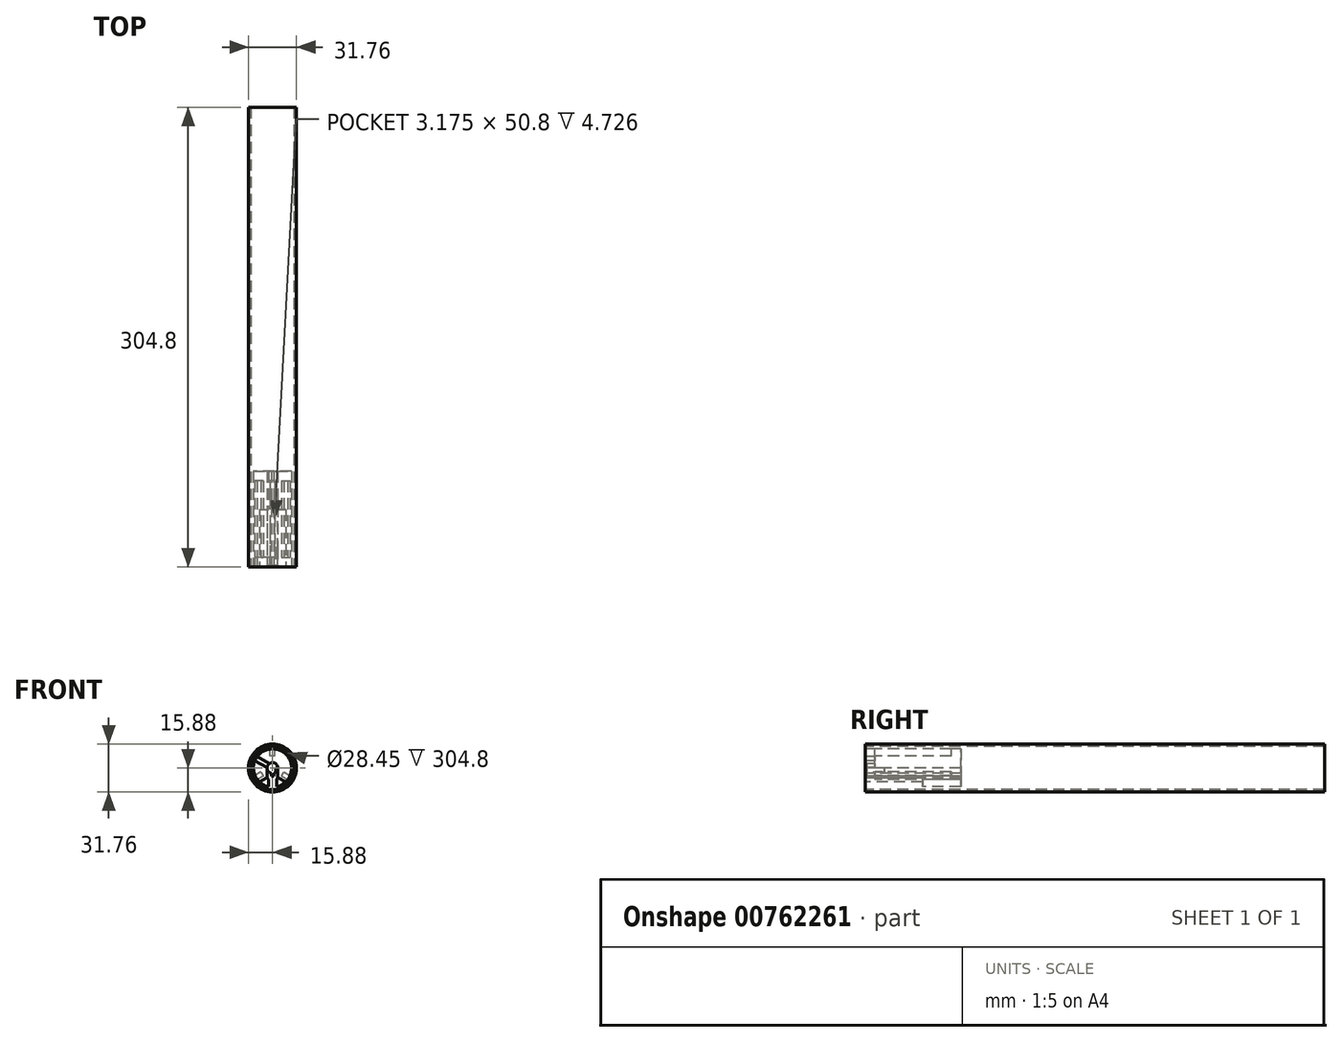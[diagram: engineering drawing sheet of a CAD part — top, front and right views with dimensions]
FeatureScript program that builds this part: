
annotation { "Feature Type Name" : "Feature", "Feature Type Description" : "" }
export const myFeature = defineFeature(function(context is Context, id is Id, definition is map)
    precondition{}
    {
        {
            var Q0;
            Q0=qCreatedBy(makeId("Front.planeOp"),FACE);
            var sketch = newSketch(context, id + "F0", { "sketchPlane" : qUnion([Q0])});
            skCircle(sketch, "E0", {"center": v(0, 0) * mm, "radius": 15.88 * mm});
            skCircle(sketch, "E1", {"center": v(0, 0) * mm, "radius": 14.22 * mm});
            skSolve(sketch);
        }
        {
            var Q0;
            Q0=makeQuery(id+"F0.imprint","IMPRINT",FACE,{"disambiguationData":[TD([[makeQuery(id+"F0.imprint","IMPRINT",EDGE,{"derivedFrom":sQuery(id+"F0.wireOp",EDGE,"E0")}),1.0]])]});
            extrude(context, id + "F1", {"entities" : qUnion([Q0]), "oppositeDirection" : true, "depth" : 304.8 * mm, "offsetDistance" : 25.4 * mm});
        }
        {
            var Q0;
            Q0=qCreatedBy(makeId("Front.planeOp"),FACE);
            var sketch = newSketch(context, id + "F2", { "sketchPlane" : qUnion([Q0])});
            skCircle(sketch, "E2", {"center": v(0, 0) * mm, "radius": 12.7 * mm});
            skCircle(sketch, "E3.0.0", {"center": v(0, 0) * mm, "radius": 15.88 * mm});
            skCircle(sketch, "E4.0", {"center": v(0, 0) * mm, "radius": 14.22 * mm});
            skLineSegment(sketch, "E5", {"start": v(0, 14.22) * mm, "end": v(0, 7.87) * mm});
            skLineSegment(sketch, "E6", {"start": v(0, 7.87) * mm, "end": v(-1.59, 7.87) * mm});
            skLineSegment(sketch, "E7", {"start": v(0, 7.87) * mm, "end": v(1.59, 7.87) * mm});
            skLineSegment(sketch, "E8", {"start": v(-1.59, 7.87) * mm, "end": v(-1.59, 14.14) * mm});
            skLineSegment(sketch, "E9", {"start": v(1.59, 7.87) * mm, "end": v(1.59, 14.14) * mm});
            skLineSegment(sketch, "E10", {"start": v(-1.59, 14.14) * mm, "end": v(1.59, 14.14) * mm});
            skLineSegment(sketch, "E11.1.0", {"start": v(-6.03, -5.31) * mm, "end": v(-11.45, -8.44) * mm});
            skLineSegment(sketch, "E11.1.1", {"start": v(-6.82, -3.94) * mm, "end": v(-6.03, -5.31) * mm});
            skLineSegment(sketch, "E11.1.2", {"start": v(-6.82, -3.94) * mm, "end": v(-7.61, -2.56) * mm});
            skLineSegment(sketch, "E11.1.3", {"start": v(-7.61, -2.56) * mm, "end": v(-13.04, -5.7) * mm});
            skLineSegment(sketch, "E11.1.4", {"start": v(-11.45, -8.44) * mm, "end": v(-13.04, -5.7) * mm});
            skLineSegment(sketch, "E11.2.0", {"start": v(7.61, -2.56) * mm, "end": v(13.04, -5.7) * mm});
            skLineSegment(sketch, "E11.2.1", {"start": v(6.82, -3.94) * mm, "end": v(7.61, -2.56) * mm});
            skLineSegment(sketch, "E11.2.2", {"start": v(6.82, -3.94) * mm, "end": v(6.03, -5.31) * mm});
            skLineSegment(sketch, "E11.2.3", {"start": v(6.03, -5.31) * mm, "end": v(11.45, -8.44) * mm});
            skLineSegment(sketch, "E11.2.4", {"start": v(13.04, -5.7) * mm, "end": v(11.45, -8.44) * mm});
            skCircle(sketch, "E12", {"center": v(0, 0) * mm, "radius": 3.56 * mm});
            skLineSegment(sketch, "E13", {"start": v(3.56, 0) * mm, "end": v(3.56, -12.2) * mm});
            skLineSegment(sketch, "E14", {"start": v(-3.56, 0) * mm, "end": v(-3.56, -12.2) * mm});
            skLineSegment(sketch, "E15", {"start": v(0, -2.16) * mm, "end": v(0.77, -2.16) * mm});
            skLineSegment(sketch, "E16", {"start": v(0.77, -2.16) * mm, "end": v(0.77, -5.34) * mm});
            skLineSegment(sketch, "E17", {"start": v(0.77, -5.34) * mm, "end": v(0, -5.34) * mm});
            skLineSegment(sketch, "E18", {"start": v(0, -2.16) * mm, "end": v(-0.75, -2.16) * mm});
            skLineSegment(sketch, "E19", {"start": v(-0.75, -2.16) * mm, "end": v(-0.75, -5.34) * mm});
            skLineSegment(sketch, "E20", {"start": v(-0.75, -5.34) * mm, "end": v(0, -5.34) * mm});
            skLineSegment(sketch, "E21", {"start": v(-3.08, 1.78) * mm, "end": v(-2.57, 1.49) * mm});
            skCircle(sketch, "E22", {"center": v(0, 0) * mm, "radius": 2.97 * mm});
            skLineSegment(sketch, "E23", {"start": v(-1.78, 2.86) * mm, "end": v(-1.38, 2.63) * mm});
            skLineSegment(sketch, "E24", {"start": v(-3.37, 0.11) * mm, "end": v(-2.97, -0.12) * mm});
            skLineSegment(sketch, "E25", {"start": v(-1.78, 2.86) * mm, "end": v(-10.12, 7.68) * mm});
            skLineSegment(sketch, "E26", {"start": v(-3.37, 0.11) * mm, "end": v(-11.7, 4.93) * mm});
            skLineSegment(sketch, "E27.trimOffspring", {"start": v(-2.57, 1.49) * mm, "end": v(-3.08, 1.78) * mm});
            skLineSegment(sketch, "E28", {"start": v(3.56, 0) * mm, "end": v(2.29, 0) * mm});
            skLineSegment(sketch, "E29", {"start": v(2.29, 0) * mm, "end": v(2.29, -12.5) * mm});
            skLineSegment(sketch, "E30", {"start": v(8.74, -9.22) * mm, "end": v(3.56, -6.2) * mm});
            skPoint(sketch, "E30.startSnap0", {"position": v(8.74, -6.88) * mm});
            skLineSegment(sketch, "E31", {"start": v(3.56, -6.2) * mm, "end": v(3.56, -12.2) * mm});
            skLineSegment(sketch, "E32", {"start": v(-8.74, -9.22) * mm, "end": v(-3.56, -6.23) * mm});
            skPoint(sketch, "E32.startSnap0", {"position": v(-8.74, -6.88) * mm});
            skLineSegment(sketch, "E33", {"start": v(-3.56, -6.23) * mm, "end": v(-3.56, -12.2) * mm});
            skLineSegment(sketch, "E34", {"start": v(3.56, -6.2) * mm, "end": v(2.75, -7.58) * mm});
            skLineSegment(sketch, "E35", {"start": v(2.75, -7.58) * mm, "end": v(3.56, -8.05) * mm});
            skLineSegment(sketch, "E36", {"start": v(-3.56, -6.23) * mm, "end": v(-2.75, -7.62) * mm});
            skLineSegment(sketch, "E37", {"start": v(-2.75, -7.62) * mm, "end": v(-3.56, -8.09) * mm});
            skLineSegment(sketch, "E38", {"start": v(-2.75, -7.62) * mm, "end": v(-2.75, -12.4) * mm});
            skLineSegment(sketch, "E39", {"start": v(2.75, -7.58) * mm, "end": v(2.75, -12.4) * mm});
            skSolve(sketch);
        }
        {
            var Q0;
            {var subQ1=sQuery(id+"F2.wireOp",EDGE,"E6");Q0=makeQuery(id+"F2.imprint","IMPRINT",FACE,{"disambiguationData":[TD([[makeQuery(id+"F2.imprint","IMPRINT",EDGE,{"derivedFrom":subQ1}),1.0]])]});}
            var Q1;
            {var subQ4=sQuery(id+"F2.wireOp",EDGE,"E15");Q1=makeQuery(id+"F2.imprint","IMPRINT",FACE,{"disambiguationData":[TD([[makeQuery(id+"F2.imprint","IMPRINT",EDGE,{"derivedFrom":subQ4}),1.0]])]});}
            var Q2;
            {var subQ0=sQuery(id+"F2.wireOp",EDGE,"E17");Q2=makeQuery(id+"F2.imprint","IMPRINT",FACE,{"disambiguationData":[TD([[makeQuery(id+"F2.imprint","IMPRINT",EDGE,{"derivedFrom":subQ0}),-1.0]])]});}
            var Q3;
            {var subQ1=sQuery(id+"F2.wireOp",EDGE,"E15");Q3=makeQuery(id+"F2.imprint","IMPRINT",FACE,{"disambiguationData":[TD([[makeQuery(id+"F2.imprint","IMPRINT",EDGE,{"derivedFrom":subQ1}),-1.0]])]});}
            var Q4;
            {var subQ0=sQuery(id+"F2.wireOp",EDGE,"E13");Q4=makeQuery(id+"F2.imprint","IMPRINT",FACE,{"disambiguationData":[TD([[makeQuery(id+"F2.imprint","IMPRINT",EDGE,{"derivedFrom":subQ0}),-1.0]])]});}
            var Q5;
            {var subQ1=sQuery(id+"F2.wireOp",EDGE,"E11.1.1");Q5=makeQuery(id+"F2.imprint","IMPRINT",FACE,{"disambiguationData":[TD([[makeQuery(id+"F2.imprint","IMPRINT",EDGE,{"derivedFrom":subQ1}),-1.0]])]});}
            var Q6;
            {var subQ5=sQuery(id+"F2.wireOp",EDGE,"E7");Q6=makeQuery(id+"F2.imprint","IMPRINT",FACE,{"disambiguationData":[TD([[makeQuery(id+"F2.imprint","IMPRINT",EDGE,{"derivedFrom":subQ5}),1.0]])]});}
            var Q7;
            {var subQ5=sQuery(id+"F2.wireOp",EDGE,"E6");Q7=makeQuery(id+"F2.imprint","IMPRINT",FACE,{"disambiguationData":[TD([[makeQuery(id+"F2.imprint","IMPRINT",EDGE,{"derivedFrom":subQ5}),-1.0]])]});}
            var Q8;
            {var subQ1=sQuery(id+"F2.wireOp",EDGE,"E11.2.1");Q8=makeQuery(id+"F2.imprint","IMPRINT",FACE,{"disambiguationData":[TD([[makeQuery(id+"F2.imprint","IMPRINT",EDGE,{"derivedFrom":subQ1}),-1.0]])]});}
            var Q9;
            {var subQ0=sQuery(id+"F2.wireOp",EDGE,"E25");var subQ1=sQuery(id+"F2.wireOp",EDGE,"E2");var subQ2=makeQuery(id+"F2.imprint","INTERSECT",VERTEX,{"derivedFrom":[subQ1,subQ0]});Q9=makeQuery(id+"F2.imprint","IMPRINT",FACE,{"disambiguationData":[TD([[makeQuery(id+"F2.imprint","IMPRINT",EDGE,{"disambiguationData":[TD([[subQ2,-1.0]])],"derivedFrom":subQ1}),1.0]])]});}
            var Q10;
            {var subQ0=sQuery(id+"F2.wireOp",EDGE,"E23");Q10=makeQuery(id+"F2.imprint","IMPRINT",FACE,{"disambiguationData":[TD([[makeQuery(id+"F2.imprint","IMPRINT",EDGE,{"derivedFrom":subQ0}),1.0]])]});}
            var Q11;
            {var subQ0=sQuery(id+"F2.wireOp",EDGE,"E23");Q11=makeQuery(id+"F2.imprint","IMPRINT",FACE,{"disambiguationData":[TD([[makeQuery(id+"F2.imprint","IMPRINT",EDGE,{"derivedFrom":subQ0}),-1.0]])]});}
            var Q12;
            {var subQ1=sQuery(id+"F2.wireOp",EDGE,"E24");Q12=makeQuery(id+"F2.imprint","IMPRINT",FACE,{"disambiguationData":[TD([[makeQuery(id+"F2.imprint","IMPRINT",EDGE,{"derivedFrom":subQ1}),1.0]])]});}
            var Q13;
            {var subQ0=sQuery(id+"F2.wireOp",EDGE,"E24");Q13=makeQuery(id+"F2.imprint","IMPRINT",FACE,{"disambiguationData":[TD([[makeQuery(id+"F2.imprint","IMPRINT",EDGE,{"derivedFrom":subQ0}),-1.0]])]});}
            var Q14;
            {var subQ0=sQuery(id+"F2.wireOp",EDGE,"E19");var subQ1=sQuery(id+"F2.wireOp",EDGE,"E12");var subQ2=makeQuery(id+"F2.imprint","INTERSECT",VERTEX,{"derivedFrom":[subQ1,subQ0]});Q14=makeQuery(id+"F2.imprint","IMPRINT",FACE,{"disambiguationData":[TD([[makeQuery(id+"F2.imprint","IMPRINT",EDGE,{"disambiguationData":[TD([[subQ2,-1.0]])],"derivedFrom":subQ1}),1.0]])]});}
            var Q15;
            {var subQ0=sQuery(id+"F2.wireOp",EDGE,"E11.1.1");Q15=makeQuery(id+"F2.imprint","IMPRINT",FACE,{"disambiguationData":[TD([[makeQuery(id+"F2.imprint","IMPRINT",EDGE,{"derivedFrom":subQ0}),1.0]])]});}
            var Q16;
            {var subQ0=sQuery(id+"F2.wireOp",EDGE,"E28");var subQ1=sQuery(id+"F2.wireOp",EDGE,"E22");var subQ2=makeQuery(id+"F2.imprint","INTERSECT",VERTEX,{"derivedFrom":[subQ1,subQ0]});Q16=makeQuery(id+"F2.imprint","IMPRINT",FACE,{"disambiguationData":[TD([[makeQuery(id+"F2.imprint","IMPRINT",EDGE,{"disambiguationData":[TD([[subQ2,1.0]])],"derivedFrom":subQ1}),1.0]])]});}
            var Q17;
            {var subQ0=sQuery(id+"F2.wireOp",EDGE,"E28");var subQ5=sQuery(id+"F2.wireOp",EDGE,"E22");var subQ7=makeQuery(id+"F2.imprint","INTERSECT",VERTEX,{"derivedFrom":[subQ5,subQ0]});Q17=makeQuery(id+"F2.imprint","IMPRINT",FACE,{"disambiguationData":[TD([[makeQuery(id+"F2.imprint","IMPRINT",EDGE,{"disambiguationData":[TD([[subQ7,1.0]])],"derivedFrom":subQ5}),-1.0]])]});}
            var Q18;
            {var subQ0=sQuery(id+"F2.wireOp",EDGE,"E16");var subQ1=sQuery(id+"F2.wireOp",EDGE,"E12");var subQ2=makeQuery(id+"F2.imprint","INTERSECT",VERTEX,{"derivedFrom":[subQ1,subQ0]});Q18=makeQuery(id+"F2.imprint","IMPRINT",FACE,{"disambiguationData":[TD([[makeQuery(id+"F2.imprint","IMPRINT",EDGE,{"disambiguationData":[TD([[subQ2,-1.0]])],"derivedFrom":subQ1}),1.0]])]});}
            var Q19;
            {var subQ5=sQuery(id+"F2.wireOp",EDGE,"E14");Q19=makeQuery(id+"F2.imprint","IMPRINT",FACE,{"disambiguationData":[TD([[makeQuery(id+"F2.imprint","IMPRINT",EDGE,{"derivedFrom":subQ5}),1.0]])]});}
            var Q20;
            {var subQ0=sQuery(id+"F2.wireOp",EDGE,"E32");Q20=makeQuery(id+"F2.imprint","IMPRINT",FACE,{"disambiguationData":[TD([[makeQuery(id+"F2.imprint","IMPRINT",EDGE,{"derivedFrom":subQ0}),-1.0]])]});}
            var Q21;
            {var subQ4=sQuery(id+"F2.wireOp",EDGE,"E37");Q21=makeQuery(id+"F2.imprint","IMPRINT",FACE,{"disambiguationData":[TD([[makeQuery(id+"F2.imprint","IMPRINT",EDGE,{"derivedFrom":subQ4}),1.0]])]});}
            var Q22;
            {var subQ0=sQuery(id+"F2.wireOp",EDGE,"E36");Q22=makeQuery(id+"F2.imprint","IMPRINT",FACE,{"disambiguationData":[TD([[makeQuery(id+"F2.imprint","IMPRINT",EDGE,{"derivedFrom":subQ0}),-1.0]])]});}
            var Q23;
            {var subQ0=sQuery(id+"F2.wireOp",EDGE,"E34");Q23=makeQuery(id+"F2.imprint","IMPRINT",FACE,{"disambiguationData":[TD([[makeQuery(id+"F2.imprint","IMPRINT",EDGE,{"derivedFrom":subQ0}),1.0]])]});}
            var Q24;
            {var subQ4=sQuery(id+"F2.wireOp",EDGE,"E35");Q24=makeQuery(id+"F2.imprint","IMPRINT",FACE,{"disambiguationData":[TD([[makeQuery(id+"F2.imprint","IMPRINT",EDGE,{"derivedFrom":subQ4}),-1.0]])]});}
            var Q25;
            {var subQ0=sQuery(id+"F2.wireOp",EDGE,"E30");Q25=makeQuery(id+"F2.imprint","IMPRINT",FACE,{"disambiguationData":[TD([[makeQuery(id+"F2.imprint","IMPRINT",EDGE,{"derivedFrom":subQ0}),1.0]])]});}
            extrude(context, id + "F3", {"entities" : qUnion([Q0, Q1, Q2, Q3, Q4, Q5, Q6, Q7, Q8, Q9, Q10, Q11, Q12, Q13, Q14, Q15, Q16, Q17, Q18, Q19, Q20, Q21, Q22, Q23, Q24, Q25]), "oppositeDirection" : true, "depth" : 63.5 * mm, "offsetDistance" : 25.4 * mm});
        }
        {
            var Q0;
            {var subQ5=sQuery(id+"F2.wireOp",EDGE,"E6");Q0=makeQuery(id+"F2.imprint","IMPRINT",FACE,{"disambiguationData":[TD([[makeQuery(id+"F2.imprint","IMPRINT",EDGE,{"derivedFrom":subQ5}),-1.0]])]});}
            var Q1;
            {var subQ5=sQuery(id+"F2.wireOp",EDGE,"E7");Q1=makeQuery(id+"F2.imprint","IMPRINT",FACE,{"disambiguationData":[TD([[makeQuery(id+"F2.imprint","IMPRINT",EDGE,{"derivedFrom":subQ5}),1.0]])]});}
            var Q2;
            {var subQ1=sQuery(id+"F2.wireOp",EDGE,"E11.1.1");Q2=makeQuery(id+"F2.imprint","IMPRINT",FACE,{"disambiguationData":[TD([[makeQuery(id+"F2.imprint","IMPRINT",EDGE,{"derivedFrom":subQ1}),-1.0]])]});}
            var Q3;
            {var subQ1=sQuery(id+"F2.wireOp",EDGE,"E11.2.1");Q3=makeQuery(id+"F2.imprint","IMPRINT",FACE,{"disambiguationData":[TD([[makeQuery(id+"F2.imprint","IMPRINT",EDGE,{"derivedFrom":subQ1}),-1.0]])]});}
            extrude(context, id + "F4", {"entities" : qUnion([Q0, Q1, Q2, Q3]), "operationType" : NewBodyOperationType.REMOVE, "oppositeDirection" : true, "depth" : 57.15 * mm, "offsetDistance" : 25.4 * mm});
        }
        {
            var Q0;
            {var subQ5=sQuery(id+"F2.wireOp",EDGE,"E6");Q0=makeQuery(id+"F2.imprint","IMPRINT",FACE,{"disambiguationData":[TD([[makeQuery(id+"F2.imprint","IMPRINT",EDGE,{"derivedFrom":subQ5}),-1.0]])]});}
            var Q1;
            {var subQ5=sQuery(id+"F2.wireOp",EDGE,"E7");Q1=makeQuery(id+"F2.imprint","IMPRINT",FACE,{"disambiguationData":[TD([[makeQuery(id+"F2.imprint","IMPRINT",EDGE,{"derivedFrom":subQ5}),1.0]])]});}
            var Q2;
            {var subQ1=sQuery(id+"F2.wireOp",EDGE,"E11.1.1");Q2=makeQuery(id+"F2.imprint","IMPRINT",FACE,{"disambiguationData":[TD([[makeQuery(id+"F2.imprint","IMPRINT",EDGE,{"derivedFrom":subQ1}),-1.0]])]});}
            var Q3;
            {var subQ1=sQuery(id+"F2.wireOp",EDGE,"E11.2.1");Q3=makeQuery(id+"F2.imprint","IMPRINT",FACE,{"disambiguationData":[TD([[makeQuery(id+"F2.imprint","IMPRINT",EDGE,{"derivedFrom":subQ1}),-1.0]])]});}
            extrude(context, id + "F5", {"entities" : qUnion([Q0, Q1, Q2, Q3]), "operationType" : NewBodyOperationType.ADD, "oppositeDirection" : true, "depth" : 6.35 * mm, "offsetDistance" : 25.4 * mm});
        }
        {
            var Q0;
            {var subQ0=sQuery(id+"F2.wireOp",EDGE,"E13");Q0=makeQuery(id+"F2.imprint","IMPRINT",FACE,{"disambiguationData":[TD([[makeQuery(id+"F2.imprint","IMPRINT",EDGE,{"derivedFrom":subQ0}),-1.0]])]});}
            var Q1;
            {var subQ4=sQuery(id+"F2.wireOp",EDGE,"E15");Q1=makeQuery(id+"F2.imprint","IMPRINT",FACE,{"disambiguationData":[TD([[makeQuery(id+"F2.imprint","IMPRINT",EDGE,{"derivedFrom":subQ4}),1.0]])]});}
            var Q2;
            {var subQ0=sQuery(id+"F2.wireOp",EDGE,"E17");Q2=makeQuery(id+"F2.imprint","IMPRINT",FACE,{"disambiguationData":[TD([[makeQuery(id+"F2.imprint","IMPRINT",EDGE,{"derivedFrom":subQ0}),-1.0]])]});}
            var Q3;
            {var subQ1=sQuery(id+"F2.wireOp",EDGE,"E15");Q3=makeQuery(id+"F2.imprint","IMPRINT",FACE,{"disambiguationData":[TD([[makeQuery(id+"F2.imprint","IMPRINT",EDGE,{"derivedFrom":subQ1}),-1.0]])]});}
            var Q4;
            {var subQ0=sQuery(id+"F2.wireOp",EDGE,"E24");Q4=makeQuery(id+"F2.imprint","IMPRINT",FACE,{"disambiguationData":[TD([[makeQuery(id+"F2.imprint","IMPRINT",EDGE,{"derivedFrom":subQ0}),-1.0]])]});}
            var Q5;
            {var subQ0=sQuery(id+"F2.wireOp",EDGE,"E19");var subQ1=sQuery(id+"F2.wireOp",EDGE,"E12");var subQ2=makeQuery(id+"F2.imprint","INTERSECT",VERTEX,{"derivedFrom":[subQ1,subQ0]});Q5=makeQuery(id+"F2.imprint","IMPRINT",FACE,{"disambiguationData":[TD([[makeQuery(id+"F2.imprint","IMPRINT",EDGE,{"disambiguationData":[TD([[subQ2,-1.0]])],"derivedFrom":subQ1}),1.0]])]});}
            var Q6;
            {var subQ0=sQuery(id+"F2.wireOp",EDGE,"E23");Q6=makeQuery(id+"F2.imprint","IMPRINT",FACE,{"disambiguationData":[TD([[makeQuery(id+"F2.imprint","IMPRINT",EDGE,{"derivedFrom":subQ0}),1.0]])]});}
            var Q7;
            {var subQ0=sQuery(id+"F2.wireOp",EDGE,"E23");Q7=makeQuery(id+"F2.imprint","IMPRINT",FACE,{"disambiguationData":[TD([[makeQuery(id+"F2.imprint","IMPRINT",EDGE,{"derivedFrom":subQ0}),-1.0]])]});}
            var Q8;
            {var subQ1=sQuery(id+"F2.wireOp",EDGE,"E24");Q8=makeQuery(id+"F2.imprint","IMPRINT",FACE,{"disambiguationData":[TD([[makeQuery(id+"F2.imprint","IMPRINT",EDGE,{"derivedFrom":subQ1}),1.0]])]});}
            var Q9;
            {var subQ0=sQuery(id+"F2.wireOp",EDGE,"E28");var subQ1=sQuery(id+"F2.wireOp",EDGE,"E22");var subQ2=makeQuery(id+"F2.imprint","INTERSECT",VERTEX,{"derivedFrom":[subQ1,subQ0]});Q9=makeQuery(id+"F2.imprint","IMPRINT",FACE,{"disambiguationData":[TD([[makeQuery(id+"F2.imprint","IMPRINT",EDGE,{"disambiguationData":[TD([[subQ2,1.0]])],"derivedFrom":subQ1}),1.0]])]});}
            var Q10;
            {var subQ0=sQuery(id+"F2.wireOp",EDGE,"E28");var subQ5=sQuery(id+"F2.wireOp",EDGE,"E22");var subQ7=makeQuery(id+"F2.imprint","INTERSECT",VERTEX,{"derivedFrom":[subQ5,subQ0]});Q10=makeQuery(id+"F2.imprint","IMPRINT",FACE,{"disambiguationData":[TD([[makeQuery(id+"F2.imprint","IMPRINT",EDGE,{"disambiguationData":[TD([[subQ7,1.0]])],"derivedFrom":subQ5}),-1.0]])]});}
            var Q11;
            {var subQ0=sQuery(id+"F2.wireOp",EDGE,"E16");var subQ1=sQuery(id+"F2.wireOp",EDGE,"E12");var subQ2=makeQuery(id+"F2.imprint","INTERSECT",VERTEX,{"derivedFrom":[subQ1,subQ0]});Q11=makeQuery(id+"F2.imprint","IMPRINT",FACE,{"disambiguationData":[TD([[makeQuery(id+"F2.imprint","IMPRINT",EDGE,{"disambiguationData":[TD([[subQ2,-1.0]])],"derivedFrom":subQ1}),1.0]])]});}
            var Q12;
            {var subQ5=sQuery(id+"F2.wireOp",EDGE,"E14");Q12=makeQuery(id+"F2.imprint","IMPRINT",FACE,{"disambiguationData":[TD([[makeQuery(id+"F2.imprint","IMPRINT",EDGE,{"derivedFrom":subQ5}),1.0]])]});}
            extrude(context, id + "F6", {"entities" : qUnion([Q0, Q1, Q2, Q3, Q4, Q5, Q6, Q7, Q8, Q9, Q10, Q11, Q12]), "operationType" : NewBodyOperationType.REMOVE, "oppositeDirection" : true, "depth" : 1.02 * mm, "offsetDistance" : 25.4 * mm});
        }
        {
            var Q0;
            {var subQ0=sQuery(id+"F2.wireOp",EDGE,"E25");var subQ1=sQuery(id+"F2.wireOp",EDGE,"E2");var subQ2=makeQuery(id+"F2.imprint","INTERSECT",VERTEX,{"derivedFrom":[subQ1,subQ0]});Q0=makeQuery(id+"F2.imprint","IMPRINT",FACE,{"disambiguationData":[TD([[makeQuery(id+"F2.imprint","IMPRINT",EDGE,{"disambiguationData":[TD([[subQ2,-1.0]])],"derivedFrom":subQ1}),1.0]])]});}
            extrude(context, id + "F7", {"entities" : qUnion([Q0]), "operationType" : NewBodyOperationType.REMOVE, "oppositeDirection" : true, "depth" : 6.35 * mm, "offsetDistance" : 25.4 * mm});
        }
        {
            var Q0;
            {var subQ0=sQuery(id+"F2.wireOp",EDGE,"E28");var subQ1=sQuery(id+"F2.wireOp",EDGE,"E22");var subQ2=makeQuery(id+"F2.imprint","INTERSECT",VERTEX,{"derivedFrom":[subQ1,subQ0]});Q0=makeQuery(id+"F2.imprint","IMPRINT",FACE,{"disambiguationData":[TD([[makeQuery(id+"F2.imprint","IMPRINT",EDGE,{"disambiguationData":[TD([[subQ2,1.0]])],"derivedFrom":subQ1}),1.0]])]});}
            var Q1;
            {var subQ0=sQuery(id+"F2.wireOp",EDGE,"E28");var subQ5=sQuery(id+"F2.wireOp",EDGE,"E22");var subQ7=makeQuery(id+"F2.imprint","INTERSECT",VERTEX,{"derivedFrom":[subQ5,subQ0]});Q1=makeQuery(id+"F2.imprint","IMPRINT",FACE,{"disambiguationData":[TD([[makeQuery(id+"F2.imprint","IMPRINT",EDGE,{"disambiguationData":[TD([[subQ7,1.0]])],"derivedFrom":subQ5}),-1.0]])]});}
            var Q2;
            {var subQ0=sQuery(id+"F2.wireOp",EDGE,"E13");Q2=makeQuery(id+"F2.imprint","IMPRINT",FACE,{"disambiguationData":[TD([[makeQuery(id+"F2.imprint","IMPRINT",EDGE,{"derivedFrom":subQ0}),-1.0]])]});}
            extrude(context, id + "F8", {"entities" : qUnion([Q0, Q1, Q2]), "operationType" : NewBodyOperationType.REMOVE, "oppositeDirection" : true, "depth" : 12.7 * mm, "offsetDistance" : 25.4 * mm});
        }
        {
            var Q0;
            {var subQ0=sQuery(id+"F2.wireOp",EDGE,"E32");Q0=makeQuery(id+"F2.imprint","IMPRINT",FACE,{"disambiguationData":[TD([[makeQuery(id+"F2.imprint","IMPRINT",EDGE,{"derivedFrom":subQ0}),-1.0]])]});}
            var Q1;
            {var subQ0=sQuery(id+"F2.wireOp",EDGE,"E36");Q1=makeQuery(id+"F2.imprint","IMPRINT",FACE,{"disambiguationData":[TD([[makeQuery(id+"F2.imprint","IMPRINT",EDGE,{"derivedFrom":subQ0}),-1.0]])]});}
            var Q2;
            {var subQ4=sQuery(id+"F2.wireOp",EDGE,"E37");Q2=makeQuery(id+"F2.imprint","IMPRINT",FACE,{"disambiguationData":[TD([[makeQuery(id+"F2.imprint","IMPRINT",EDGE,{"derivedFrom":subQ4}),1.0]])]});}
            var Q3;
            {var subQ0=sQuery(id+"F2.wireOp",EDGE,"E34");Q3=makeQuery(id+"F2.imprint","IMPRINT",FACE,{"disambiguationData":[TD([[makeQuery(id+"F2.imprint","IMPRINT",EDGE,{"derivedFrom":subQ0}),1.0]])]});}
            var Q4;
            {var subQ4=sQuery(id+"F2.wireOp",EDGE,"E35");Q4=makeQuery(id+"F2.imprint","IMPRINT",FACE,{"disambiguationData":[TD([[makeQuery(id+"F2.imprint","IMPRINT",EDGE,{"derivedFrom":subQ4}),-1.0]])]});}
            var Q5;
            {var subQ0=sQuery(id+"F2.wireOp",EDGE,"E30");Q5=makeQuery(id+"F2.imprint","IMPRINT",FACE,{"disambiguationData":[TD([[makeQuery(id+"F2.imprint","IMPRINT",EDGE,{"derivedFrom":subQ0}),1.0]])]});}
            extrude(context, id + "F9", {"entities" : qUnion([Q0, Q1, Q2, Q3, Q4, Q5]), "operationType" : NewBodyOperationType.REMOVE, "oppositeDirection" : true, "depth" : 38.1 * mm, "offsetDistance" : 25.4 * mm});
        }
    });
